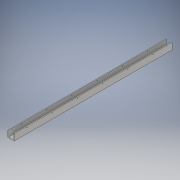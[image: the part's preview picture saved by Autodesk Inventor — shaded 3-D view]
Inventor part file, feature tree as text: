
AUTODESK INVENTOR PART (.ipt)
format: ipt  version: 2018 (Build 220112000, 112)  size: 143,872 bytes
history: native  units: in
note: dims shown in document units (in); Inventor stores cm internally (conversion verified against a paired STEP export)
features: extrude x3, sketch x3
ambient origin geometry x8: Origin, YZ Plane, XZ Plane, XY Plane, X Axis, Y Axis, Z Axis, Center Point
bodies: Solid1 (feature_tree)
feature tree (6):
  extrude  "Extrusion1"  Depth=1.0in
  extrude  "Extrusion2"  Depth=25.0in TaperAngle=0.0deg
  extrude  "Extrusion3"  Depth=25.0in
  sketch  "Sketch1"  dims[d0=1.0in d1=1.0in]
  sketch  "Sketch2"  dims[d2=0.125in d3=25.0in d4=0.0in]
  sketch  "Sketch3"  dims[d5=0.263in d6=0.143in d8=3.0in d9=4.0in d11=4.0in d12=4.0in d13=4.0in d14=4.0in d15=0.104in d16=25.0in d17=0.0in d18=0.75in d19=25.0in d20=0.0in]
